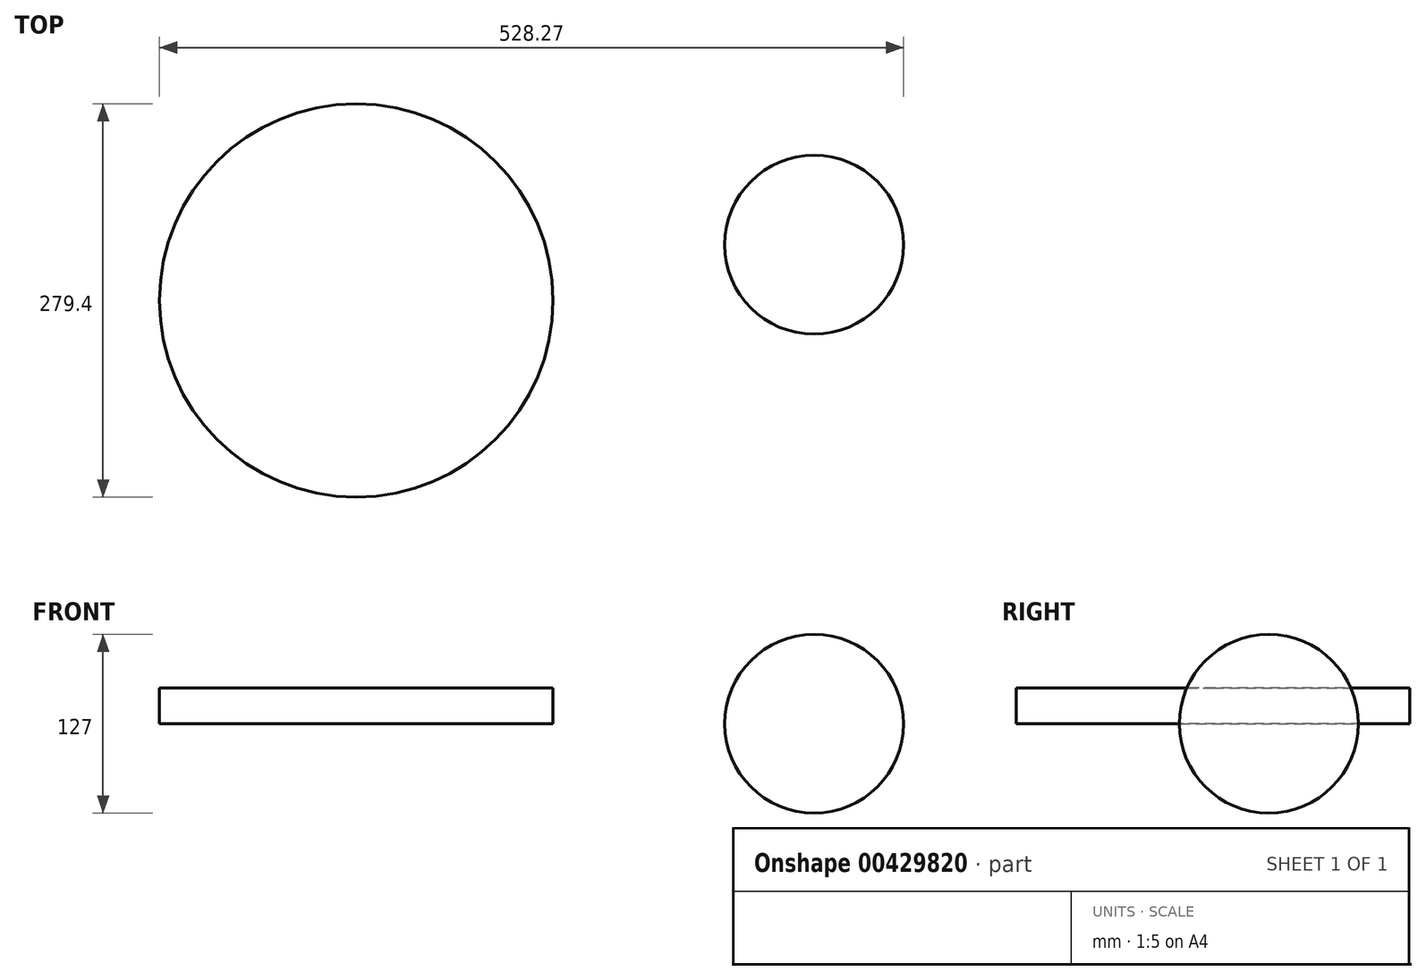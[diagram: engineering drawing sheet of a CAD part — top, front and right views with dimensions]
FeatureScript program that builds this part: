
annotation { "Feature Type Name" : "Feature", "Feature Type Description" : "" }
export const myFeature = defineFeature(function(context is Context, id is Id, definition is map)
    precondition{}
    {
        {
            var Q0;
            Q0=qCreatedBy(makeId("Top.planeOp"),FACE);
            var sketch = newSketch(context, id + "F0", { "sketchPlane" : qUnion([Q0])});
            skCircle(sketch, "E0", {"center": v(-44.84, 35.38) * mm, "radius": 139.7 * mm});
            skSolve(sketch);
        }
        {
            var Q0;
            Q0=makeQuery(id+"F0.imprint","IMPRINT",FACE,{"disambiguationData":[TD([[makeQuery(id+"F0.imprint","IMPRINT",EDGE,{"derivedFrom":sQuery(id+"F0.wireOp",EDGE,"E0")}),1.0]])]});
            extrude(context, id + "F1", {"entities" : qUnion([Q0]), "depth" : 25.4 * mm});
        }
        {
            var Q0;
            Q0=qCreatedBy(makeId("Top.planeOp"),FACE);
            var sketch = newSketch(context, id + "F2", { "sketchPlane" : qUnion([Q0])});
            skArc(sketch, "E1", {"start": v(343.73, 74.96) * mm, "mid": v(280.23, 138.46) * mm, "end": v(216.73, 74.96) * mm});
            skLineSegment(sketch, "E2", {"start": v(216.73, 74.96) * mm, "end": v(343.73, 74.96) * mm});
            skSolve(sketch);
        }
        {
            var Q0;
            Q0=makeQuery(id+"F2.imprint","IMPRINT",FACE,{"disambiguationData":[TD([[makeQuery(id+"F2.imprint","IMPRINT",EDGE,{"derivedFrom":sQuery(id+"F2.wireOp",EDGE,"E1")}),1.0]])]});
            var Q1;
            Q1=sQuery(id+"F2.wireOp",EDGE,"E2");
            revolve(context, id + "F3", {"entities" : qUnion([Q0]), "axis" : qUnion([Q1]), "revolveType" : RevolveType.FULL});
        }
    });
